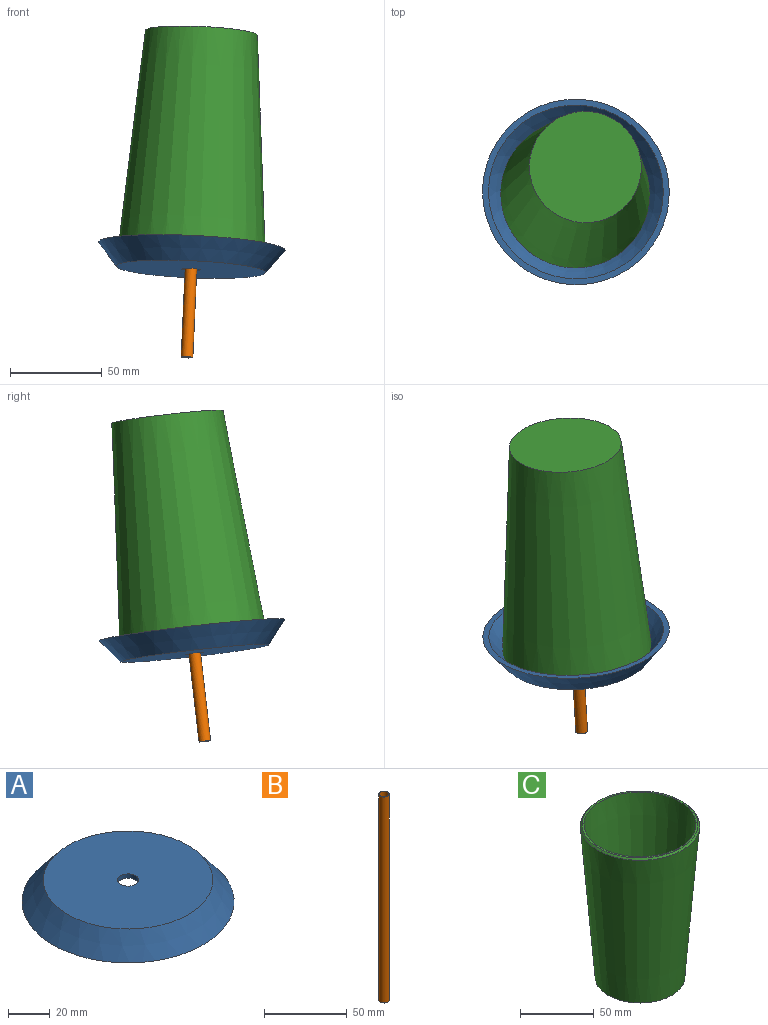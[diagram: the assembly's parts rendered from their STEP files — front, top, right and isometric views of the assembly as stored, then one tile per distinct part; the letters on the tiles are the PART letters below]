
ASSEMBLY  parts=3 mates=2
PART A: 6 faces, bbox 101.6x101.6x12.7 mm
  f0: plane 101.6x101.6mm, normal (0,0,-1), area 1005mm2, adj f2,f4
  f1: plane 81.28x81.28mm, normal (0,0,1), area 5107.6mm2, adj f2,f5
  f2: cone r=40.64mm half-angle=38.7deg, axis (0,0,-1), area 4672.1mm2, adj f0,f1
  f3: plane 78.84x78.84mm, normal (0,0,-1), area 4800.6mm2, adj f4,f5
  f4: cone r=38.66mm half-angle=38.7deg, axis (0,0,-1), area 3554.8mm2, adj f0,f3
  f5: cylinder r=5.08mm len=10.16mm, axis (0,0,1), area 81.1mm2, adj f1,f3
PART B: 4 faces, bbox 6.4x6.4x152.4 mm
  f0: cylinder r=3.17mm len=152.4mm, axis (0,0,-1), area 3040.2mm2, adj f1,f2
  f1: plane 6.35x6.35mm, normal (0,0,1), area 4.9mm2, adj f0,f3
  f2: plane 6.35x6.35mm, normal (0,0,-1), area 4.9mm2, adj f0,f3
  f3: cylinder r=2.92mm len=152.4mm, axis (0,0,1), area 2797mm2, adj f1,f2
PART C: 6 faces, bbox 81.1x81.1x127 mm
  f0: plane 60.96x60.96mm, normal (0,0,-1), area 2918.6mm2, adj f2
  f1: plane 78.74x78.74mm, normal (0,0,1), area 311mm2, adj f4,f5
  f2: cone r=40.64mm half-angle=4.6deg, axis (0,0,1), area 28142.4mm2, adj f0,f5
  f3: plane 56.27x56.27mm, normal (0,0,1), area 2486.8mm2, adj f4
  f4: cone r=38.11mm half-angle=4.6deg, axis (0,0,1), area 25977.7mm2, adj f1,f3
  f5: cone r=39.37mm half-angle=42.7deg, axis (0,0,-1), area 432.5mm2, adj f1,f2
PLACE A rot(axis=(0.93,-0.36,0),173deg) t=(-58.68,-28.14,-82.09)mm
PLACE B rot(axis=(0.93,-0.36,0),173deg) t=(-57.46,-24.94,-54.36)mm
PLACE C rot(axis=(0.93,-0.36,0),173deg) t=(-58.57,-27.85,-79.57)mm fixed
MATE slider B.f0 <-> C.f2  axis (0.04,0.11,0.99) through (-57.46,-24.94,-54.36)mm
MATE cylindrical A.f5 <-> C.f2  axis (-0.04,-0.11,-0.99) through (-58.57,-27.85,-79.57)mm
